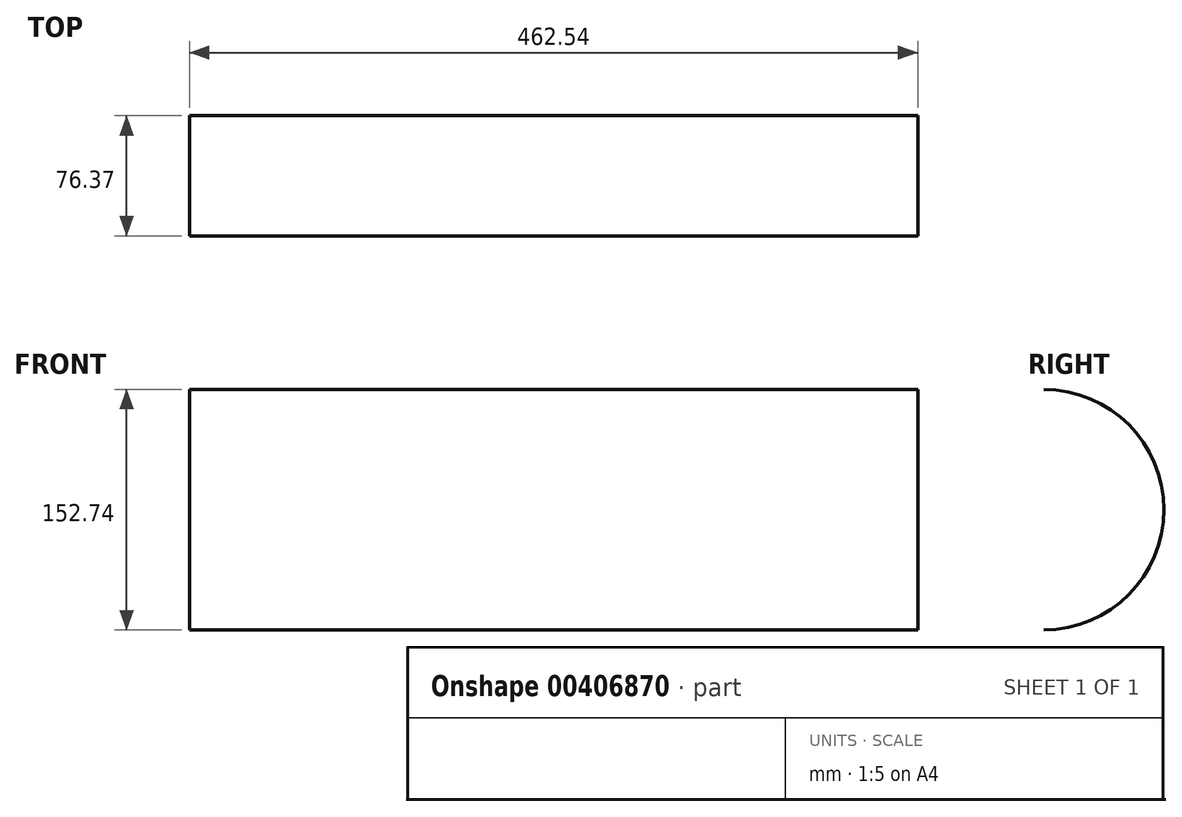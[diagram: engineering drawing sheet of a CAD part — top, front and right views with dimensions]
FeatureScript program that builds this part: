
annotation { "Feature Type Name" : "Feature", "Feature Type Description" : "" }
export const myFeature = defineFeature(function(context is Context, id is Id, definition is map)
    precondition{}
    {
        {
            var Q0;
            Q0=qCreatedBy(makeId("Right.planeOp"),FACE);
            var sketch = newSketch(context, id + "F0", { "sketchPlane" : qUnion([Q0])});
            skArc(sketch, "E0", {"start": v(0, 76.37) * mm, "mid": v(76.37, 0) * mm, "end": v(0, -76.37) * mm});
            skSolve(sketch);
        }
        {
            var Q0;
            Q0=sQuery(id+"F0.wireOp",EDGE,"E0");
            extrude(context, id + "F1", {"bodyType" : ToolBodyType.SURFACE, "surfaceEntities" : qUnion([Q0]), "depth" : 277.2 * mm, "hasSecondDirection" : true, "secondDirectionOppositeDirection" : true, "secondDirectionDepth" : 185.34 * mm});
        }
    });
